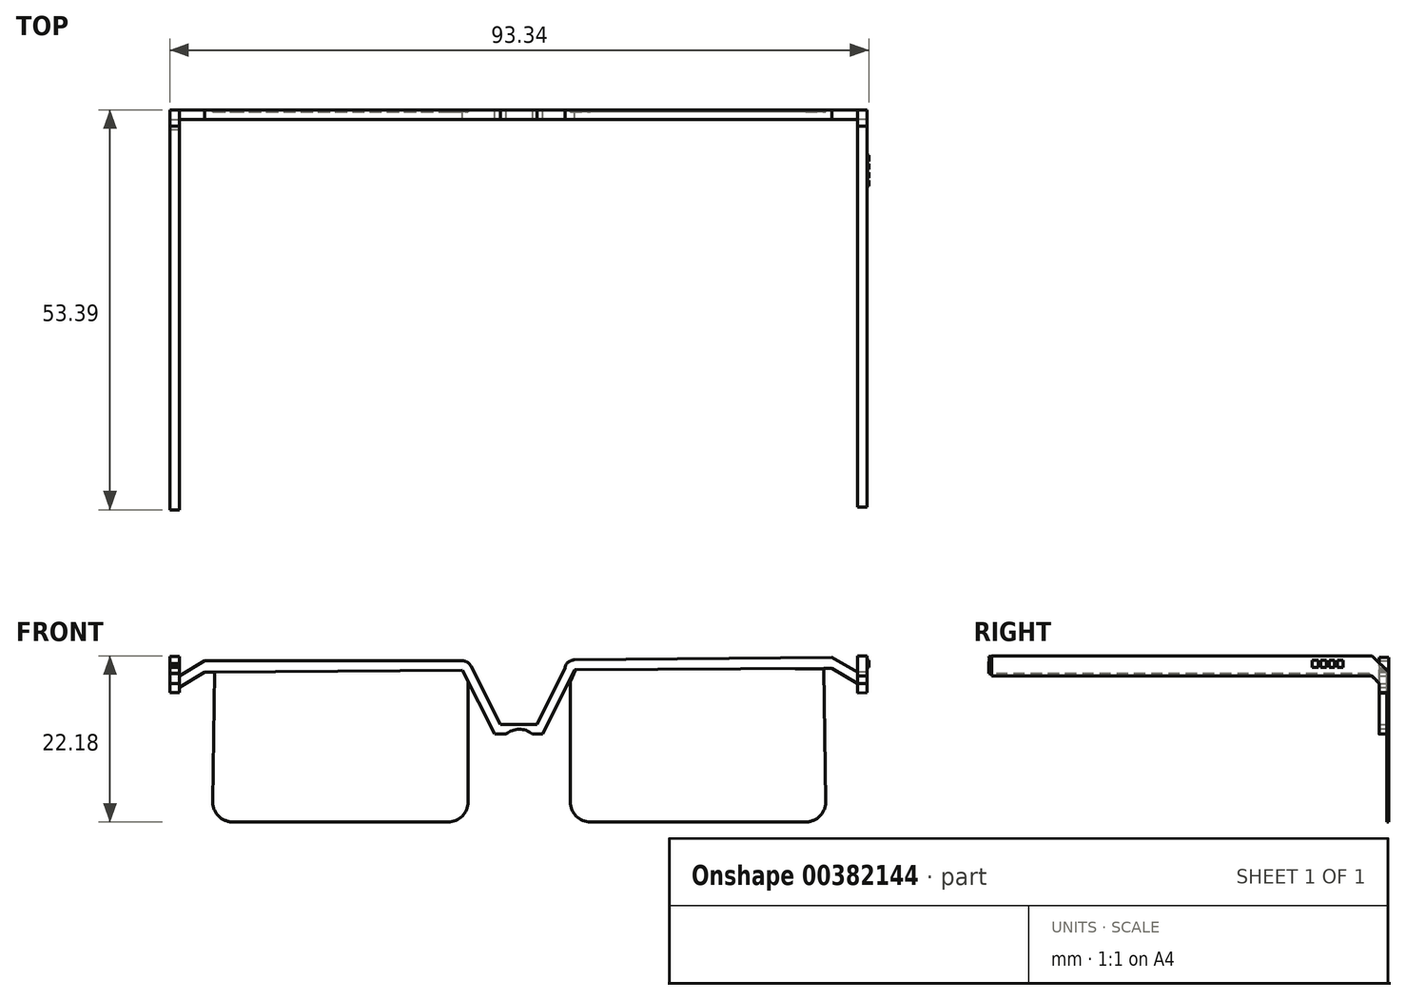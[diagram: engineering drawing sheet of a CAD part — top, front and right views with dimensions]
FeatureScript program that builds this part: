
annotation { "Feature Type Name" : "Feature", "Feature Type Description" : "" }
export const myFeature = defineFeature(function(context is Context, id is Id, definition is map)
    precondition{}
    {
        {
            var Q0;
            Q0=qCreatedBy(makeId("Front.planeOp"),FACE);
            var sketch = newSketch(context, id + "F0", { "sketchPlane" : qUnion([Q0])});
            skLineSegment(sketch, "E0", {"start": v(-56.12, 30.07) * mm, "end": v(-21.72, 30.07) * mm});
            skArc(sketch, "E1", {"start": v(-20.6, 29.37) * mm, "mid": v(-21.06, 29.88) * mm, "end": v(-21.72, 30.07) * mm});
            skLineSegment(sketch, "E2", {"start": v(-20.6, 29.37) * mm, "end": v(-16.62, 21.55) * mm});
            skLineSegment(sketch, "E3", {"start": v(-56.12, 30.07) * mm, "end": v(-59.5, 28.02) * mm});
            skLineSegment(sketch, "E4", {"start": v(-59.5, 26.54) * mm, "end": v(-56.12, 28.58) * mm});
            skLineSegment(sketch, "E5", {"start": v(-56.12, 28.58) * mm, "end": v(-55.01, 28.58) * mm});
            skLineSegment(sketch, "E6", {"start": v(-17.9, 21.28) * mm, "end": v(-21.72, 28.8) * mm});
            skLineSegment(sketch, "E7", {"start": v(-17.9, 21.28) * mm, "end": v(-17.4, 20.28) * mm});
            skLineSegment(sketch, "E8", {"start": v(-55.01, 28.58) * mm, "end": v(-21.72, 28.8) * mm});
            skLineSegment(sketch, "E9", {"start": v(-59.5, 28.02) * mm, "end": v(-59.5, 26.54) * mm});
            skLineSegment(sketch, "E10.MirrorCS", {"start": v(27.62, 30.54) * mm, "end": v(-6.77, 30.18) * mm});
            skLineSegment(sketch, "E11.MirrorCS", {"start": v(26.53, 29.05) * mm, "end": v(-6.75, 28.88) * mm});
            skLineSegment(sketch, "E12.MirrorCS", {"start": v(-8.03, 29.16) * mm, "end": v(-11.78, 21.58) * mm});
            skLineSegment(sketch, "E13.MirrorCS", {"start": v(-10.5, 21.32) * mm, "end": v(-6.75, 28.88) * mm});
            skLineSegment(sketch, "E14.MirrorCS", {"start": v(27.62, 30.54) * mm, "end": v(31.04, 28.54) * mm});
            skLineSegment(sketch, "E15.MirrorCS", {"start": v(31.05, 27.05) * mm, "end": v(27.64, 29.06) * mm});
            skLineSegment(sketch, "E16.MirrorCS", {"start": v(27.64, 29.06) * mm, "end": v(26.53, 29.05) * mm});
            skLineSegment(sketch, "E17.MirrorCS", {"start": v(31.04, 28.54) * mm, "end": v(31.05, 27.05) * mm});
            skArc(sketch, "E18.MirrorCS", {"start": v(-8.03, 29.16) * mm, "mid": v(-7.58, 29.9) * mm, "end": v(-6.77, 30.18) * mm});
            skLineSegment(sketch, "E19.MirrorCS", {"start": v(-10.5, 21.32) * mm, "end": v(-10.99, 20.32) * mm});
            skLineSegment(sketch, "E20", {"start": v(-17.4, 20.28) * mm, "end": v(-10.99, 20.32) * mm});
            skLineSegment(sketch, "E21", {"start": v(-56.12, 30.07) * mm, "end": v(-56.12, 28.58) * mm});
            skLineSegment(sketch, "E22", {"start": v(-21.72, 30.07) * mm, "end": v(-21.72, 28.8) * mm});
            skLineSegment(sketch, "E23", {"start": v(-17.9, 21.28) * mm, "end": v(-16.62, 21.55) * mm});
            skLineSegment(sketch, "E24", {"start": v(-11.78, 21.58) * mm, "end": v(-10.5, 21.32) * mm});
            skLineSegment(sketch, "E25", {"start": v(-6.77, 30.18) * mm, "end": v(-6.75, 28.88) * mm});
            skLineSegment(sketch, "E26", {"start": v(-16.62, 21.55) * mm, "end": v(-11.78, 21.58) * mm});
            skPoint(sketch, "E27.centerSnap0", {"position": v(-14.2, 20.3) * mm});
            skLineSegment(sketch, "E28", {"start": v(-14.2, 18.12) * mm, "end": v(-14.22, 23.7) * mm});
            skSolve(sketch);
        }
        {
            var Q0;
            Q0=qCreatedBy(makeId("Front.planeOp"),FACE);
            var sketch = newSketch(context, id + "F1", { "sketchPlane" : qUnion([Q0])});
            skLineSegment(sketch, "E29", {"start": v(-54.82, 29.03) * mm, "end": v(-21.74, 29.03) * mm});
            skLineSegment(sketch, "E30", {"start": v(-21.74, 29.03) * mm, "end": v(-20.96, 27.3) * mm});
            skPoint(sketch, "E31", {"position": v(-14.13, 21.55) * mm});
            skArc(sketch, "E32", {"start": v(-52.39, 8.55) * mm, "mid": v(-54.3, 9.35) * mm, "end": v(-55.06, 11.27) * mm});
            skLineSegment(sketch, "E33", {"start": v(-52.39, 8.55) * mm, "end": v(-23.64, 8.55) * mm});
            skLineSegment(sketch, "E34", {"start": v(-55.06, 11.27) * mm, "end": v(-54.82, 29.03) * mm});
            skArc(sketch, "E35.MirrorCS", {"start": v(-23.64, 8.55) * mm, "mid": v(-21.62, 9.47) * mm, "end": v(-20.98, 11.59) * mm});
            skLineSegment(sketch, "E36", {"start": v(-20.96, 27.3) * mm, "end": v(-20.96, 11.23) * mm});
            skLineSegment(sketch, "E37.MirrorCS", {"start": v(-7.3, 27.3) * mm, "end": v(-7.3, 11.23) * mm});
            skLineSegment(sketch, "E38.MirrorCS", {"start": v(-6.52, 29.03) * mm, "end": v(-7.3, 27.3) * mm});
            skLineSegment(sketch, "E39.MirrorCS", {"start": v(26.55, 29.03) * mm, "end": v(-6.52, 29.03) * mm});
            skArc(sketch, "E40.MirrorCS", {"start": v(-4.63, 8.55) * mm, "mid": v(-6.64, 9.47) * mm, "end": v(-7.28, 11.59) * mm});
            skLineSegment(sketch, "E41.MirrorCS", {"start": v(24.12, 8.55) * mm, "end": v(-4.63, 8.55) * mm});
            skArc(sketch, "E42.MirrorCS", {"start": v(24.12, 8.55) * mm, "mid": v(26.03, 9.35) * mm, "end": v(26.8, 11.27) * mm});
            skLineSegment(sketch, "E43.MirrorCS", {"start": v(26.8, 11.27) * mm, "end": v(26.55, 29.03) * mm});
            skSolve(sketch);
        }
        {
            var Q0;
            Q0=makeQuery(id+"F0.imprint","IMPRINT",FACE,{"disambiguationData":[TD([[makeQuery(id+"F0.imprint","IMPRINT",EDGE,{"derivedFrom":sQuery(id+"F0.wireOp",EDGE,"E3")}),1.0]])]});
            var Q1;
            Q1=makeQuery(id+"F0.imprint","IMPRINT",FACE,{"disambiguationData":[TD([[makeQuery(id+"F0.imprint","IMPRINT",EDGE,{"derivedFrom":sQuery(id+"F0.wireOp",EDGE,"E10.MirrorCS")}),1.0]])]});
            var Q2;
            Q2=makeQuery(id+"F0.imprint","IMPRINT",FACE,{"disambiguationData":[TD([[makeQuery(id+"F0.imprint","IMPRINT",EDGE,{"derivedFrom":sQuery(id+"F0.wireOp",EDGE,"E0")}),-1.0]])]});
            var Q3;
            Q3=makeQuery(id+"F0.imprint","IMPRINT",FACE,{"disambiguationData":[TD([[makeQuery(id+"F0.imprint","IMPRINT",EDGE,{"derivedFrom":sQuery(id+"F0.wireOp",EDGE,"E1")}),1.0]])]});
            var Q4;
            Q4=makeQuery(id+"F0.imprint","IMPRINT",FACE,{"disambiguationData":[TD([[makeQuery(id+"F0.imprint","IMPRINT",EDGE,{"derivedFrom":sQuery(id+"F0.wireOp",EDGE,"E12.MirrorCS")}),1.0]])]});
            var Q5;
            {var subQ0=sQuery(id+"F0.wireOp",EDGE,"E27");var subQ1=sQuery(id+"F0.wireOp",EDGE,"E20");var subQ2=makeQuery(id+"F0.imprint","INTERSECT",VERTEX,{"disambiguationData":[OD(0.0)],"derivedFrom":[subQ1,subQ0]});Q5=makeQuery(id+"F0.imprint","IMPRINT",FACE,{"disambiguationData":[TD([[makeQuery(id+"F0.imprint","IMPRINT",EDGE,{"disambiguationData":[TD([[subQ2,-1.0]])],"derivedFrom":subQ1}),1.0]])]});}
            var Q6;
            {var subQ1=sQuery(id+"F0.wireOp",EDGE,"E7");Q6=makeQuery(id+"F0.imprint","IMPRINT",FACE,{"disambiguationData":[TD([[makeQuery(id+"F0.imprint","IMPRINT",EDGE,{"derivedFrom":subQ1}),1.0]])]});}
            extrude(context, id + "F2", {"entities" : qUnion([Q0, Q1, Q2, Q3, Q4, Q5, Q6]), "depth" : 1.27 * mm});
        }
        {
            var Q0;
            Q0 = qSketchRegion(id + "F1", true);
            extrude(context, id + "F3", {"entities" : qUnion([Q0]), "operationType" : NewBodyOperationType.ADD, "depth" : 0.25 * mm});
        }
        {
            var Q0;
            Q0=makeQuery(id+"F2.opExtrude","SWEPT_FACE",FACE,{"disambiguationData":[OSD([sQuery(id+"F0.wireOp",EDGE,"E9")])]});
            var sketch = newSketch(context, id + "F4", { "sketchPlane" : qUnion([Q0])});
            skLineSegment(sketch, "E44", {"start": v(1.27, 28.54) * mm, "end": v(0, 28.54) * mm});
            skLineSegment(sketch, "E45", {"start": v(1.27, 28.54) * mm, "end": v(1.27, 27.05) * mm});
            skLineSegment(sketch, "E46", {"start": v(0, 27.05) * mm, "end": v(1.27, 27.05) * mm});
            skLineSegment(sketch, "E47", {"start": v(0, 27.05) * mm, "end": v(0, 28.54) * mm});
            skLineSegment(sketch, "E48", {"start": v(0, 28.54) * mm, "end": v(2.14, 30.66) * mm});
            skLineSegment(sketch, "E49", {"start": v(0, 27.05) * mm, "end": v(0, 25.81) * mm});
            skLineSegment(sketch, "E50", {"start": v(0, 25.81) * mm, "end": v(2.59, 28.38) * mm});
            skLineSegment(sketch, "E51", {"start": v(2.14, 30.66) * mm, "end": v(20.43, 30.66) * mm});
            skLineSegment(sketch, "E52", {"start": v(2.59, 28.38) * mm, "end": v(20.43, 28.38) * mm});
            skLineSegment(sketch, "E53", {"start": v(1.27, 27.05) * mm, "end": v(1.27, 25.81) * mm});
            skLineSegment(sketch, "E54", {"start": v(0, 25.81) * mm, "end": v(1.27, 25.81) * mm});
            skLineSegment(sketch, "E55", {"start": v(20.43, 30.66) * mm, "end": v(53.39, 30.66) * mm});
            skLineSegment(sketch, "E56", {"start": v(53.39, 30.66) * mm, "end": v(53.39, 28.38) * mm});
            skLineSegment(sketch, "E57", {"start": v(53.39, 28.38) * mm, "end": v(20.43, 28.38) * mm});
            skPoint(sketch, "E58.12.internal.snap0", {"position": v(53.39, 29.52) * mm});
            skFitSpline(sketch, "E59", {"points": [v(53.39, 30.66) * mm, v(56, 30.66) * mm, v(57.85, 29.42) * mm, v(58.66, 27.28) * mm, v(59.22, 24.92) * mm, v(59.4, 23.47) * mm, v(59.22, 21.63) * mm, v(58.32, 19.66) * mm, v(56.31, 20.22) * mm, v(56.4, 21.97) * mm, v(56.44, 23.51) * mm, v(56.18, 24.88) * mm, v(55.33, 26.17) * mm, v(54.56, 26.98) * mm, v(53.78, 27.88) * mm, v(53.39, 28.38) * mm, v(53.39, 28.58) * mm, v(53.39, 29.52) * mm, v(53.39, 29.73) * mm, v(53.39, 30.66) * mm]});
            skLineSegment(sketch, "E60", {"start": v(2.59, 28.38) * mm, "end": v(2.59, 30.66) * mm});
            skSolve(sketch);
        }
        {
            var Q0;
            Q0=makeQuery(id+"F2.opExtrude","SWEPT_FACE",FACE,{"disambiguationData":[OSD([sQuery(id+"F0.wireOp",EDGE,"E17.MirrorCS")])]});
            var sketch = newSketch(context, id + "F5", { "sketchPlane" : qUnion([Q0])});
            skLineSegment(sketch, "E61", {"start": v(0, 28.21) * mm, "end": v(-2.17, 30.39) * mm});
            skLineSegment(sketch, "E62", {"start": v(0, 28.21) * mm, "end": v(-1.27, 28.21) * mm});
            skLineSegment(sketch, "E63", {"start": v(-1.27, 28.21) * mm, "end": v(-1.27, 26.73) * mm});
            skLineSegment(sketch, "E64", {"start": v(-1.27, 26.73) * mm, "end": v(0, 26.73) * mm});
            skLineSegment(sketch, "E65", {"start": v(0, 26.73) * mm, "end": v(0, 28.21) * mm});
            skLineSegment(sketch, "E66", {"start": v(0, 28.21) * mm, "end": v(0, 25.46) * mm});
            skPoint(sketch, "E66.endSnap0", {"position": v(0, 27.47) * mm});
            skLineSegment(sketch, "E67", {"start": v(0, 25.46) * mm, "end": v(-1.27, 26.73) * mm});
            skLineSegment(sketch, "E68", {"start": v(-1.27, 26.73) * mm, "end": v(-2.23, 27.74) * mm});
            skLineSegment(sketch, "E69", {"start": v(-2.17, 30.39) * mm, "end": v(-20.41, 30.39) * mm});
            skLineSegment(sketch, "E70", {"start": v(-2.23, 27.74) * mm, "end": v(-20.41, 27.74) * mm});
            skLineSegment(sketch, "E71", {"start": v(-20.41, 27.74) * mm, "end": v(-53.03, 27.74) * mm});
            skLineSegment(sketch, "E72", {"start": v(-53.03, 27.74) * mm, "end": v(-53.03, 30.39) * mm});
            skLineSegment(sketch, "E73", {"start": v(-53.03, 30.39) * mm, "end": v(-20.41, 30.39) * mm});
            skLineSegment(sketch, "E74", {"start": v(0, 25.46) * mm, "end": v(-1.27, 25.46) * mm});
            skLineSegment(sketch, "E75", {"start": v(-1.27, 25.46) * mm, "end": v(-1.27, 28.21) * mm});
            skFitSpline(sketch, "E76", {"points": [v(-53.03, 30.39) * mm, v(-53.1, 30.39) * mm, v(-55.76, 30.39) * mm, v(-57.6, 29.32) * mm, v(-58.76, 27.22) * mm, v(-58.89, 24.31) * mm, v(-58.41, 22.05) * mm, v(-57.13, 20.76) * mm, v(-55.6, 21.36) * mm, v(-55.85, 22.73) * mm, v(-56.36, 24.44) * mm, v(-55.85, 26.2) * mm, v(-54.74, 27) * mm, v(-53.84, 27.52) * mm, v(-53.03, 27.74) * mm, v(-53.03, 27.74) * mm, v(-53.03, 29.07) * mm, v(-53.03, 30.39) * mm]});
            skLineSegment(sketch, "E77", {"start": v(-2.23, 30.39) * mm, "end": v(-2.23, 27.74) * mm});
            skSolve(sketch);
        }
        {
            var Q0;
            Q0 = qSketchRegion(id + "F5", true);
            extrude(context, id + "F6", {"entities" : qUnion([Q0]), "operationType" : NewBodyOperationType.ADD, "depth" : 1.27 * mm});
        }
        {
            var Q0;
            Q0=makeQuery(id+"F4.imprint","IMPRINT",FACE,{"disambiguationData":[TD([[makeQuery(id+"F4.imprint","IMPRINT",EDGE,{"derivedFrom":sQuery(id+"F4.wireOp",EDGE,"E52")}),1.0]])]});
            var Q1;
            {var subQ0=sQuery(id+"F4.wireOp",EDGE,"E59");var subQ1=sQuery(id+"F4.wireOp",EDGE,"E56");var subQ5=makeQuery(id+"F4.imprint","INTERSECT",VERTEX,{"disambiguationData":[OD(1.0)],"derivedFrom":[subQ1,subQ0]});Q1=makeQuery(id+"F4.imprint","IMPRINT",FACE,{"disambiguationData":[TD([[makeQuery(id+"F4.imprint","IMPRINT",EDGE,{"disambiguationData":[TD([[subQ5,-1.0]])],"derivedFrom":subQ1}),1.0]])]});}
            var Q2;
            {var subQ3=sQuery(id+"F4.wireOp",EDGE,"E44");Q2=makeQuery(id+"F4.imprint","IMPRINT",FACE,{"disambiguationData":[TD([[makeQuery(id+"F4.imprint","IMPRINT",EDGE,{"derivedFrom":subQ3}),-1.0]])]});}
            var Q3;
            {var subQ5=makeQuery(id+"F2.opExtrude","SWEPT_EDGE",EDGE,{"disambiguationData":[OSD([sQuery(id+"F0.wireOp",EDGE,"E3"),sQuery(id+"F0.wireOp",EDGE,"E9")])]});Q3=makeQuery(id+"F4.imprint","IMPRINT",FACE,{"disambiguationData":[TD([[makeQuery(id+"F4.imprint","IMPRINT",EDGE,{"derivedFrom":subQ5}),1.0]])]});}
            var Q4;
            {var subQ0=sQuery(id+"F4.wireOp",EDGE,"E44");Q4=makeQuery(id+"F4.imprint","IMPRINT",FACE,{"disambiguationData":[TD([[makeQuery(id+"F4.imprint","IMPRINT",EDGE,{"derivedFrom":subQ0}),1.0]])]});}
            var Q5;
            {var subQ0=sQuery(id+"F4.wireOp",EDGE,"E54");Q5=makeQuery(id+"F4.imprint","IMPRINT",FACE,{"disambiguationData":[TD([[makeQuery(id+"F4.imprint","IMPRINT",EDGE,{"derivedFrom":subQ0}),1.0]])]});}
            var Q6;
            {var subQ0=sQuery(id+"F4.wireOp",EDGE,"E49");var subQ1=makeQuery(id+"F2.opExtrude","SWEPT_EDGE",EDGE,{"disambiguationData":[OSD([sQuery(id+"F0.wireOp",EDGE,"E4"),sQuery(id+"F0.wireOp",EDGE,"E9")])]});var subQ2=makeQuery(id+"F4.imprint","INTERSECT",VERTEX,{"derivedFrom":[subQ1,subQ0]});Q6=makeQuery(id+"F4.imprint","IMPRINT",FACE,{"disambiguationData":[TD([[makeQuery(id+"F4.imprint","IMPRINT",EDGE,{"disambiguationData":[TD([[subQ2,-1.0]])],"derivedFrom":subQ0}),1.0]])]});}
            var Q7;
            {var subQ1=sQuery(id+"F4.wireOp",EDGE,"E46");var subQ3=sQuery(id+"F4.wireOp",EDGE,"E50");var subQ4=makeQuery(id+"F4.imprint","INTERSECT",VERTEX,{"derivedFrom":[subQ1,subQ3]});Q7=makeQuery(id+"F4.imprint","IMPRINT",FACE,{"disambiguationData":[TD([[makeQuery(id+"F4.imprint","IMPRINT",EDGE,{"disambiguationData":[TD([[subQ4,1.0]])],"derivedFrom":subQ1}),-1.0]])]});}
            var Q8;
            {var subQ1=sQuery(id+"F4.wireOp",EDGE,"E46");var subQ3=sQuery(id+"F4.wireOp",EDGE,"E50");var subQ4=makeQuery(id+"F4.imprint","INTERSECT",VERTEX,{"derivedFrom":[subQ1,subQ3]});Q8=makeQuery(id+"F4.imprint","IMPRINT",FACE,{"disambiguationData":[TD([[makeQuery(id+"F4.imprint","IMPRINT",EDGE,{"disambiguationData":[TD([[subQ4,-1.0]])],"derivedFrom":subQ1}),-1.0]])]});}
            extrude(context, id + "F7", {"entities" : qUnion([Q0, Q1, Q2, Q3, Q4, Q5, Q6, Q7, Q8]), "depth" : 1.27 * mm});
        }
        {
            var Q0;
            Q0=makeQuery(id+"F6.opExtrude","CAP_FACE",FACE,{"disambiguationData":[OSD([sQuery(id+"F5.wireOp",EDGE,"E61"),sQuery(id+"F5.wireOp",EDGE,"E66"),sQuery(id+"F5.wireOp",EDGE,"E68"),sQuery(id+"F5.wireOp",EDGE,"E69"),sQuery(id+"F5.wireOp",EDGE,"E70"),sQuery(id+"F5.wireOp",EDGE,"E71"),sQuery(id+"F5.wireOp",EDGE,"E73"),sQuery(id+"F5.wireOp",EDGE,"E74"),sQuery(id+"F5.wireOp",EDGE,"E75"),sQuery(id+"F5.wireOp",EDGE,"E76")])],"isStart":false});
            var sketch = newSketch(context, id + "F8", { "sketchPlane" : qUnion([Q0])});
            skLineSegment(sketch, "E78.bottom", {"start": v(-6.83, 29.82) * mm, "end": v(-6.06, 29.82) * mm});
            skLineSegment(sketch, "E78.top", {"start": v(-6.83, 28.83) * mm, "end": v(-6.06, 28.83) * mm});
            skLineSegment(sketch, "E78.left", {"start": v(-6.83, 29.82) * mm, "end": v(-6.83, 28.83) * mm});
            skLineSegment(sketch, "E78.right", {"start": v(-6.06, 29.82) * mm, "end": v(-6.06, 28.83) * mm});
            skLineSegment(sketch, "E79.bottom", {"start": v(-7.2, 29.82) * mm, "end": v(-7.94, 29.82) * mm});
            skLineSegment(sketch, "E79.top", {"start": v(-7.2, 28.83) * mm, "end": v(-7.94, 28.83) * mm});
            skLineSegment(sketch, "E79.left", {"start": v(-7.2, 29.82) * mm, "end": v(-7.2, 28.83) * mm});
            skLineSegment(sketch, "E79.right", {"start": v(-7.94, 29.82) * mm, "end": v(-7.94, 28.83) * mm});
            skLineSegment(sketch, "E80.bottom", {"start": v(-8.3, 29.82) * mm, "end": v(-9.06, 29.82) * mm});
            skLineSegment(sketch, "E80.top", {"start": v(-8.3, 28.83) * mm, "end": v(-9.06, 28.83) * mm});
            skLineSegment(sketch, "E80.left", {"start": v(-8.3, 29.82) * mm, "end": v(-8.3, 28.83) * mm});
            skLineSegment(sketch, "E80.right", {"start": v(-9.06, 29.82) * mm, "end": v(-9.06, 28.83) * mm});
            skLineSegment(sketch, "E81.bottom", {"start": v(-9.37, 29.82) * mm, "end": v(-10.17, 29.82) * mm});
            skLineSegment(sketch, "E81.top", {"start": v(-9.37, 28.83) * mm, "end": v(-10.17, 28.83) * mm});
            skLineSegment(sketch, "E81.left", {"start": v(-9.37, 29.82) * mm, "end": v(-9.37, 28.83) * mm});
            skLineSegment(sketch, "E81.right", {"start": v(-10.17, 29.82) * mm, "end": v(-10.17, 28.83) * mm});
            skSolve(sketch);
        }
        {
            var Q0;
            Q0=makeQuery(id+"F8.imprint","IMPRINT",FACE,{"disambiguationData":[TD([[makeQuery(id+"F8.imprint","IMPRINT",EDGE,{"derivedFrom":sQuery(id+"F8.wireOp",EDGE,"E81.bottom")}),1.0]])]});
            var Q1;
            Q1=makeQuery(id+"F8.imprint","IMPRINT",FACE,{"disambiguationData":[TD([[makeQuery(id+"F8.imprint","IMPRINT",EDGE,{"derivedFrom":sQuery(id+"F8.wireOp",EDGE,"E80.bottom")}),1.0]])]});
            var Q2;
            Q2=makeQuery(id+"F8.imprint","IMPRINT",FACE,{"disambiguationData":[TD([[makeQuery(id+"F8.imprint","IMPRINT",EDGE,{"derivedFrom":sQuery(id+"F8.wireOp",EDGE,"E79.bottom")}),1.0]])]});
            var Q3;
            Q3=makeQuery(id+"F8.imprint","IMPRINT",FACE,{"disambiguationData":[TD([[makeQuery(id+"F8.imprint","IMPRINT",EDGE,{"derivedFrom":sQuery(id+"F8.wireOp",EDGE,"E78.bottom")}),-1.0]])]});
            extrude(context, id + "F9", {"entities" : qUnion([Q0, Q1, Q2, Q3]), "operationType" : NewBodyOperationType.ADD, "depth" : 0.25 * mm});
        }
        {
            var Q0;
            Q0=makeQuery(id+"F2.opExtrude","CAP_FACE",FACE,{"disambiguationData":[OSD([sQuery(id+"F0.wireOp",EDGE,"E0"),sQuery(id+"F0.wireOp",EDGE,"E1"),sQuery(id+"F0.wireOp",EDGE,"E2"),sQuery(id+"F0.wireOp",EDGE,"E3"),sQuery(id+"F0.wireOp",EDGE,"E4"),sQuery(id+"F0.wireOp",EDGE,"E5"),sQuery(id+"F0.wireOp",EDGE,"E6"),sQuery(id+"F0.wireOp",EDGE,"E7"),sQuery(id+"F0.wireOp",EDGE,"E8"),sQuery(id+"F0.wireOp",EDGE,"E9"),sQuery(id+"F0.wireOp",EDGE,"E10.MirrorCS"),sQuery(id+"F0.wireOp",EDGE,"E11.MirrorCS"),sQuery(id+"F0.wireOp",EDGE,"E12.MirrorCS"),sQuery(id+"F0.wireOp",EDGE,"E13.MirrorCS"),sQuery(id+"F0.wireOp",EDGE,"E14.MirrorCS"),sQuery(id+"F0.wireOp",EDGE,"E15.MirrorCS"),sQuery(id+"F0.wireOp",EDGE,"E16.MirrorCS"),sQuery(id+"F0.wireOp",EDGE,"E17.MirrorCS"),sQuery(id+"F0.wireOp",EDGE,"E18.MirrorCS"),sQuery(id+"F0.wireOp",EDGE,"E19.MirrorCS"),sQuery(id+"F0.wireOp",EDGE,"E20"),sQuery(id+"F0.wireOp",EDGE,"E26")])],"isStart":false});
            var sketch = newSketch(context, id + "F10", { "sketchPlane" : qUnion([Q0])});
            skCircle(sketch, "E82", {"center": v(-14.13, 18.15) * mm, "radius": 2.79 * mm});
            skSolve(sketch);
        }
        {
            var Q0;
            Q0 = qSketchRegion(id + "F10", true);
            extrude(context, id + "F11", {"entities" : qUnion([Q0]), "operationType" : NewBodyOperationType.REMOVE, "oppositeDirection" : true, "depth" : 9.86 * mm});
        }
    });
